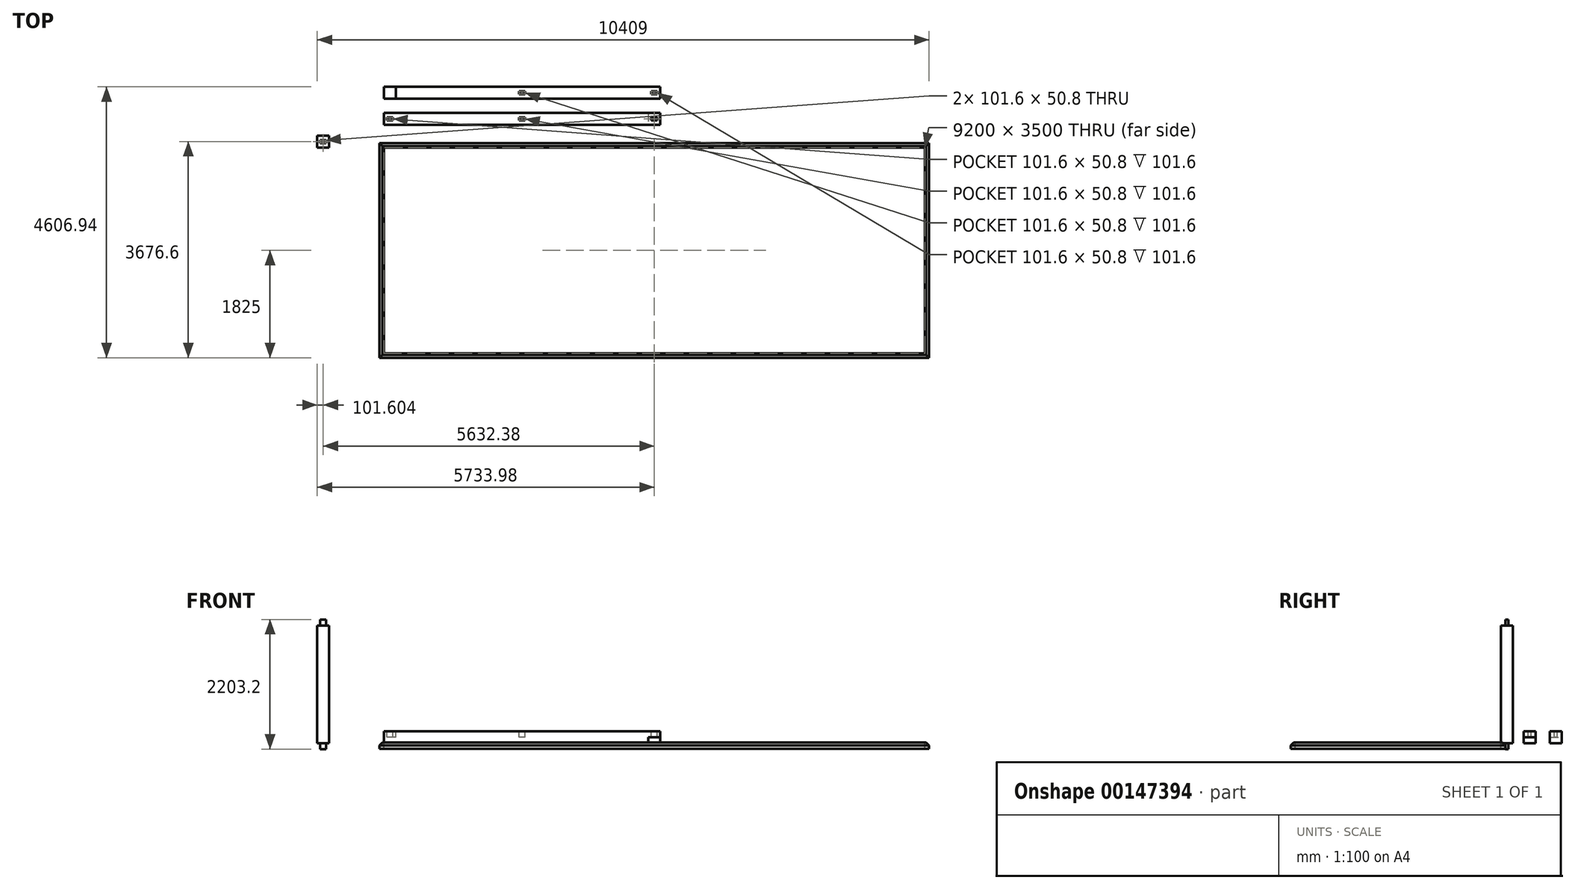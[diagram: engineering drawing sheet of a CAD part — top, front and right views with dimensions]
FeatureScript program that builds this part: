
annotation { "Feature Type Name" : "Feature", "Feature Type Description" : "" }
export const myFeature = defineFeature(function(context is Context, id is Id, definition is map)
    precondition{}
    {
        {
            var Q0;
            Q0=qCreatedBy(makeId("Top.planeOp"),FACE);
            var sketch = newSketch(context, id + "F0", { "sketchPlane" : qUnion([Q0])});
            skLineSegment(sketch, "E0.bottom", {"start": v(0, 0) * mm, "end": v(9200, 0) * mm});
            skLineSegment(sketch, "E0.top", {"start": v(0, -3500) * mm, "end": v(9200, -3500) * mm});
            skLineSegment(sketch, "E0.left", {"start": v(0, 0) * mm, "end": v(0, -3500) * mm});
            skLineSegment(sketch, "E0.right", {"start": v(9200, 0) * mm, "end": v(9200, -3500) * mm});
            skSolve(sketch);
        }
        {
            var Q0;
            Q0=qCreatedBy(makeId("Right.planeOp"),FACE);
            var sketch = newSketch(context, id + "F1", { "sketchPlane" : qUnion([Q0])});
            skLineSegment(sketch, "E1", {"start": v(0, 0) * mm, "end": v(0, 8.64) * mm});
            skLineSegment(sketch, "E2", {"start": v(0, 8.64) * mm, "end": v(25, 8.64) * mm});
            skLineSegment(sketch, "E3", {"start": v(25, 8.64) * mm, "end": v(75, -40) * mm});
            skLineSegment(sketch, "E4", {"start": v(75, -40) * mm, "end": v(75, -100) * mm});
            skLineSegment(sketch, "E5", {"start": v(75, -100) * mm, "end": v(0, -100) * mm});
            skLineSegment(sketch, "E6", {"start": v(0, -100) * mm, "end": v(0, 0) * mm});
            skSolve(sketch);
        }
        {
            var Q0;
            Q0=makeQuery(id+"F1.imprint","IMPRINT",FACE,{"disambiguationData":[TD([[makeQuery(id+"F1.imprint","IMPRINT",EDGE,{"derivedFrom":sQuery(id+"F1.wireOp",EDGE,"E1")}),-1.0]])]});
            var Q1;
            Q1=sQuery(id+"F0.wireOp",EDGE,"E0.bottom");
            var Q2;
            Q2=sQuery(id+"F0.wireOp",EDGE,"E0.right");
            var Q3;
            Q3=sQuery(id+"F0.wireOp",EDGE,"E0.top");
            var Q4;
            Q4=sQuery(id+"F0.wireOp",EDGE,"E0.left");
            sweep(context, id + "F2", {"profiles" : qUnion([Q0]), "path" : qUnion([Q1, Q2, Q3, Q4])});
        }
        {
            var Q0;
            Q0=qCreatedBy(makeId("Right.planeOp"),FACE);
            var sketch = newSketch(context, id + "F3", { "sketchPlane" : qUnion([Q0])});
            skLineSegment(sketch, "E7.bottom", {"start": v(388, 0) * mm, "end": v(591.2, 0) * mm});
            skLineSegment(sketch, "E7.top", {"start": v(388, 203.2) * mm, "end": v(591.2, 203.2) * mm});
            skLineSegment(sketch, "E7.left", {"start": v(388, 0) * mm, "end": v(388, 203.2) * mm});
            skLineSegment(sketch, "E7.right", {"start": v(591.2, 0) * mm, "end": v(591.2, 203.2) * mm});
            skSolve(sketch);
        }
        {
            var Q0;
            Q0 = qSketchRegion(id + "F3", true);
            extrude(context, id + "F4", {"entities" : qUnion([Q0]), "depth" : 4701.6 * mm});
        }
        {
            var Q0;
            Q0=makeQuery(id+"F4.opExtrude","SWEPT_FACE",FACE,{"disambiguationData":[OSD([sQuery(id+"F3.wireOp",EDGE,"E7.top")])]});
            var sketch = newSketch(context, id + "F5", { "sketchPlane" : qUnion([Q0])});
            skLineSegment(sketch, "E8", {"start": v(4701.6, 489.6) * mm, "end": v(0, 489.6) * mm, "construction": true});
            skLineSegment(sketch, "E9.bottom", {"start": v(4650.8, 515) * mm, "end": v(4549.2, 515) * mm});
            skLineSegment(sketch, "E9.top", {"start": v(4650.8, 464.2) * mm, "end": v(4549.2, 464.2) * mm});
            skLineSegment(sketch, "E9.left", {"start": v(4650.8, 515) * mm, "end": v(4650.8, 464.2) * mm});
            skLineSegment(sketch, "E9.right", {"start": v(4549.2, 515) * mm, "end": v(4549.2, 464.2) * mm});
            skLineSegment(sketch, "E10.1.0.0", {"start": v(2401.6, 464.2) * mm, "end": v(2300, 464.2) * mm});
            skLineSegment(sketch, "E10.1.0.1", {"start": v(2401.6, 515) * mm, "end": v(2401.6, 464.2) * mm});
            skLineSegment(sketch, "E10.1.0.2", {"start": v(2401.6, 515) * mm, "end": v(2300, 515) * mm});
            skLineSegment(sketch, "E10.1.0.3", {"start": v(2300, 515) * mm, "end": v(2300, 464.2) * mm});
            skLineSegment(sketch, "E10.2.0.0", {"start": v(152.4, 464.2) * mm, "end": v(50.8, 464.2) * mm});
            skLineSegment(sketch, "E10.2.0.1", {"start": v(152.4, 515) * mm, "end": v(152.4, 464.2) * mm});
            skLineSegment(sketch, "E10.2.0.2", {"start": v(152.4, 515) * mm, "end": v(50.8, 515) * mm});
            skLineSegment(sketch, "E10.2.0.3", {"start": v(50.8, 515) * mm, "end": v(50.8, 464.2) * mm});
            skLineSegment(sketch, "E10.direction1", {"start": v(4549.2, 464.2) * mm, "end": v(2300, 464.2) * mm, "construction": true});
            skLineSegment(sketch, "E11", {"start": v(2350.8, 388) * mm, "end": v(2350.8, 798.17) * mm, "construction": true});
            skSolve(sketch);
        }
        {
            var Q0;
            Q0 = qSketchRegion(id + "F5", true);
            extrude(context, id + "F6", {"entities" : qUnion([Q0]), "operationType" : NewBodyOperationType.REMOVE, "oppositeDirection" : true, "depth" : 101.6 * mm});
        }
        {
            var Q0;
            Q0=makeQuery(id+"F4.opExtrude","SWEPT_FACE",FACE,{"disambiguationData":[OSD([sQuery(id+"F3.wireOp",EDGE,"E7.bottom")])]});
            var sketch = newSketch(context, id + "F7", { "sketchPlane" : qUnion([Q0])});
            skLineSegment(sketch, "E12", {"start": v(4498.4, -591.2) * mm, "end": v(4498.4, -388) * mm});
            skSolve(sketch);
        }
        {
            var Q0;
            Q0 = qSketchRegion(id + "F7", true);
            var Q1;
            {var subQ0=sQuery(id+"F7.wireOp",EDGE,"E12");Q1=makeQuery(id+"F7.imprint","IMPRINT",FACE,{"disambiguationData":[TD([[makeQuery(id+"F7.imprint","IMPRINT",EDGE,{"derivedFrom":subQ0}),-1.0]])]});}
            extrude(context, id + "F8", {"entities" : qUnion([Q0, Q1]), "operationType" : NewBodyOperationType.REMOVE, "oppositeDirection" : true, "depth" : 101.6 * mm});
        }
        {
            var Q0;
            {var subQ0=sQuery(id+"F7.wireOp",EDGE,"E12");Q0=makeQuery(id+"F7.imprint","IMPRINT",FACE,{"disambiguationData":[TD([[makeQuery(id+"F7.imprint","IMPRINT",EDGE,{"derivedFrom":subQ0}),-1.0]])]});}
            extrude(context, id + "F9", {"entities" : qUnion([Q0]), "operationType" : NewBodyOperationType.REMOVE, "oppositeDirection" : true, "depth" : 101.6 * mm});
        }
        {
            var Q0;
            Q0=qCreatedBy(makeId("Right.planeOp"),FACE);
            var sketch = newSketch(context, id + "F10", { "sketchPlane" : qUnion([Q0])});
            skLineSegment(sketch, "E13.bottom", {"start": v(828.74, 0) * mm, "end": v(1031.94, 0) * mm});
            skLineSegment(sketch, "E13.top", {"start": v(828.74, 203.2) * mm, "end": v(1031.94, 203.2) * mm});
            skLineSegment(sketch, "E13.left", {"start": v(828.74, 0) * mm, "end": v(828.74, 203.2) * mm});
            skLineSegment(sketch, "E13.right", {"start": v(1031.94, 0) * mm, "end": v(1031.94, 203.2) * mm});
            skSolve(sketch);
        }
        {
            var Q0;
            Q0=makeQuery(id+"F10.imprint","IMPRINT",FACE,{"disambiguationData":[TD([[makeQuery(id+"F10.imprint","IMPRINT",EDGE,{"derivedFrom":sQuery(id+"F10.wireOp",EDGE,"E13.bottom")}),1.0]])]});
            extrude(context, id + "F11", {"entities" : qUnion([Q0]), "depth" : 4701.6 * mm});
        }
        {
            var Q0;
            Q0=makeQuery(id+"F11.opExtrude","SWEPT_FACE",FACE,{"disambiguationData":[OSD([sQuery(id+"F10.wireOp",EDGE,"E13.top")])]});
            var sketch = newSketch(context, id + "F12", { "sketchPlane" : qUnion([Q0])});
            skLineSegment(sketch, "E14", {"start": v(203.2, 828.74) * mm, "end": v(203.2, 1031.94) * mm});
            skSolve(sketch);
        }
        {
            var Q0;
            {var subQ0=sQuery(id+"F12.wireOp",EDGE,"E14");Q0=makeQuery(id+"F12.imprint","IMPRINT",FACE,{"disambiguationData":[TD([[makeQuery(id+"F12.imprint","IMPRINT",EDGE,{"derivedFrom":subQ0}),1.0]])]});}
            extrude(context, id + "F13", {"entities" : qUnion([Q0]), "operationType" : NewBodyOperationType.REMOVE, "oppositeDirection" : true, "depth" : 101.6 * mm});
        }
        {
            var Q0;
            Q0=makeQuery(id+"F11.opExtrude","SWEPT_FACE",FACE,{"disambiguationData":[OSD([sQuery(id+"F10.wireOp",EDGE,"E13.top")])]});
            var sketch = newSketch(context, id + "F14", { "sketchPlane" : qUnion([Q0])});
            skLineSegment(sketch, "E15", {"start": v(4701.6, 930.34) * mm, "end": v(203.2, 930.34) * mm, "construction": true});
            skLineSegment(sketch, "E16.bottom", {"start": v(4650.8, 955.74) * mm, "end": v(4549.2, 955.74) * mm});
            skLineSegment(sketch, "E16.top", {"start": v(4650.8, 904.94) * mm, "end": v(4549.2, 904.94) * mm});
            skLineSegment(sketch, "E16.left", {"start": v(4650.8, 955.74) * mm, "end": v(4650.8, 904.94) * mm});
            skLineSegment(sketch, "E16.right", {"start": v(4549.2, 955.74) * mm, "end": v(4549.2, 904.94) * mm});
            skLineSegment(sketch, "E17.1.0.0", {"start": v(2401.6, 955.74) * mm, "end": v(2300, 955.74) * mm});
            skLineSegment(sketch, "E17.1.0.1", {"start": v(2401.6, 955.74) * mm, "end": v(2401.6, 904.94) * mm});
            skLineSegment(sketch, "E17.1.0.2", {"start": v(2401.6, 904.94) * mm, "end": v(2300, 904.94) * mm});
            skLineSegment(sketch, "E17.1.0.3", {"start": v(2300, 955.74) * mm, "end": v(2300, 904.94) * mm});
            skLineSegment(sketch, "E17.direction1", {"start": v(4549.2, 955.74) * mm, "end": v(2300, 955.74) * mm, "construction": true});
            skSolve(sketch);
        }
        {
            var Q0;
            Q0 = qSketchRegion(id + "F14", true);
            extrude(context, id + "F15", {"entities" : qUnion([Q0]), "operationType" : NewBodyOperationType.REMOVE, "oppositeDirection" : true, "depth" : 101.6 * mm});
        }
        {
            var Q0;
            Q0=qCreatedBy(makeId("Top.planeOp"),FACE);
            var sketch = newSketch(context, id + "F16", { "sketchPlane" : qUnion([Q0])});
            skLineSegment(sketch, "E18.bottom", {"start": v(-930.78, 0) * mm, "end": v(-1133.98, 0) * mm});
            skLineSegment(sketch, "E18.top", {"start": v(-930.78, 203.2) * mm, "end": v(-1133.98, 203.2) * mm});
            skLineSegment(sketch, "E18.left", {"start": v(-930.78, 0) * mm, "end": v(-930.78, 203.2) * mm});
            skLineSegment(sketch, "E18.right", {"start": v(-1133.98, 0) * mm, "end": v(-1133.98, 203.2) * mm});
            skSolve(sketch);
        }
        {
            var Q0;
            Q0 = qSketchRegion(id + "F16", true);
            extrude(context, id + "F17", {"entities" : qUnion([Q0]), "depth" : 2000 * mm});
        }
        {
            var Q0;
            Q0=makeQuery(id+"F17.opExtrude","CAP_FACE",FACE,{"disambiguationData":[OSD([sQuery(id+"F16.wireOp",EDGE,"E18.bottom"),sQuery(id+"F16.wireOp",EDGE,"E18.top"),sQuery(id+"F16.wireOp",EDGE,"E18.left"),sQuery(id+"F16.wireOp",EDGE,"E18.right")])],"isStart":false});
            var sketch = newSketch(context, id + "F18", { "sketchPlane" : qUnion([Q0])});
            skLineSegment(sketch, "E19", {"start": v(-930.78, 101.6) * mm, "end": v(-1133.98, 101.6) * mm, "construction": true});
            skLineSegment(sketch, "E20.bottom", {"start": v(-981.58, 127) * mm, "end": v(-1083.18, 127) * mm});
            skLineSegment(sketch, "E20.top", {"start": v(-981.58, 76.2) * mm, "end": v(-1083.18, 76.2) * mm});
            skLineSegment(sketch, "E20.left", {"start": v(-981.58, 127) * mm, "end": v(-981.58, 76.2) * mm});
            skLineSegment(sketch, "E20.right", {"start": v(-1083.18, 127) * mm, "end": v(-1083.18, 76.2) * mm});
            skSolve(sketch);
        }
        {
            var Q0;
            Q0 = qSketchRegion(id + "F18", true);
            extrude(context, id + "F19", {"entities" : qUnion([Q0]), "operationType" : NewBodyOperationType.ADD, "depth" : 101.6 * mm});
        }
        {
            var Q0;
            Q0=makeQuery(id+"F17.opExtrude","CAP_FACE",FACE,{"disambiguationData":[OSD([sQuery(id+"F16.wireOp",EDGE,"E18.bottom"),sQuery(id+"F16.wireOp",EDGE,"E18.top"),sQuery(id+"F16.wireOp",EDGE,"E18.left"),sQuery(id+"F16.wireOp",EDGE,"E18.right")])],"isStart":true});
            var sketch = newSketch(context, id + "F20", { "sketchPlane" : qUnion([Q0])});
            skLineSegment(sketch, "E21", {"start": v(-930.78, -101.6) * mm, "end": v(-1133.98, -101.6) * mm, "construction": true});
            skLineSegment(sketch, "E22.bottom", {"start": v(-981.58, -76.2) * mm, "end": v(-1083.18, -76.2) * mm});
            skLineSegment(sketch, "E22.top", {"start": v(-981.58, -127) * mm, "end": v(-1083.18, -127) * mm});
            skLineSegment(sketch, "E22.left", {"start": v(-981.58, -76.2) * mm, "end": v(-981.58, -127) * mm});
            skLineSegment(sketch, "E22.right", {"start": v(-1083.18, -76.2) * mm, "end": v(-1083.18, -127) * mm});
            skSolve(sketch);
        }
        {
            var Q0;
            Q0 = qSketchRegion(id + "F20", true);
            extrude(context, id + "F21", {"entities" : qUnion([Q0]), "operationType" : NewBodyOperationType.ADD, "depth" : 101.6 * mm});
        }
    });
